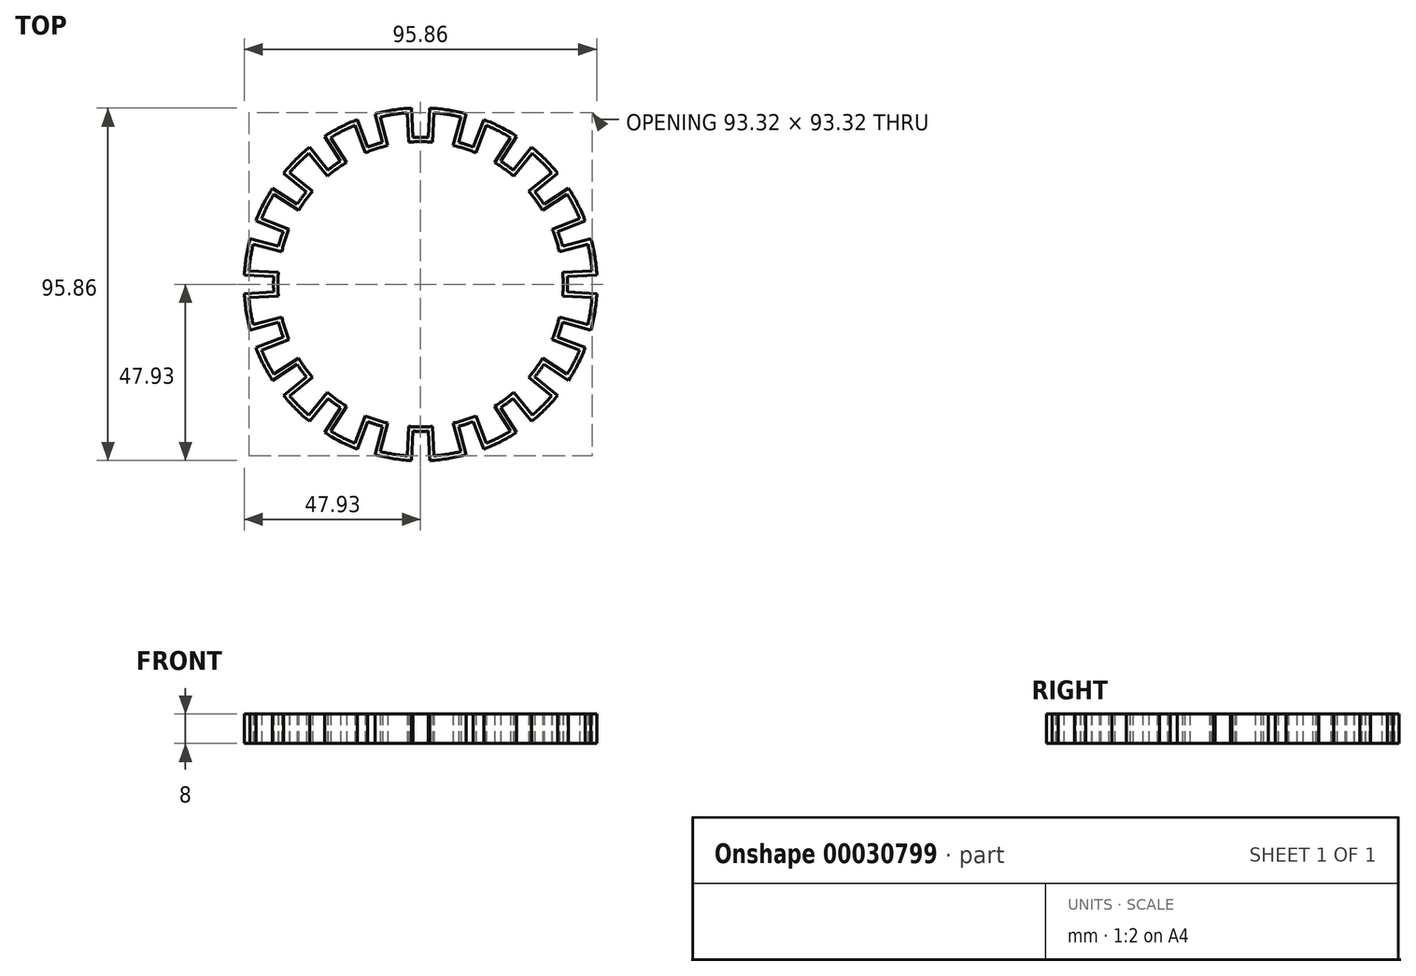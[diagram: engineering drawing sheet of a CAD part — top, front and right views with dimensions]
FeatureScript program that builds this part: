
annotation { "Feature Type Name" : "Feature", "Feature Type Description" : "" }
export const myFeature = defineFeature(function(context is Context, id is Id, definition is map)
    precondition{}
    {
        {
            var Q0;
            Q0=qCreatedBy(makeId("Top.planeOp"),FACE);
            var sketch = newSketch(context, id + "F0", { "sketchPlane" : qUnion([Q0])});
            skLineSegment(sketch, "E0", {"start": v(0, 40) * mm, "end": v(0, 0) * mm});
            skLineSegment(sketch, "E1", {"start": v(0, 0) * mm, "end": v(12.36, 38.04) * mm});
            skArc(sketch, "E2", {"start": v(12.42, 46.36) * mm, "mid": v(7.5, 47.4) * mm, "end": v(2.51, 47.93) * mm});
            skArc(sketch, "E3", {"start": v(12.36, 38.04) * mm, "mid": v(11.36, 38.35) * mm, "end": v(10.35, 38.64) * mm});
            skLineSegment(sketch, "E4", {"start": v(10.35, 38.64) * mm, "end": v(12.42, 46.36) * mm});
            skLineSegment(sketch, "E5", {"start": v(12.42, 46.36) * mm, "end": v(10.35, 38.64) * mm});
            skLineSegment(sketch, "E6", {"start": v(2.51, 47.93) * mm, "end": v(2.1, 39.95) * mm});
            skArc(sketch, "E7.trimOffspring", {"start": v(2.1, 39.95) * mm, "mid": v(1.05, 39.99) * mm, "end": v(0, 40) * mm});
            skPoint(sketch, "E8.start.orphan", {"position": v(0, 48) * mm});
            skSolve(sketch);
        }
        {
            var Q0;
            Q0 = qSketchRegion(id + "F0", true);
            extrude(context, id + "F1", {"entities" : qUnion([Q0]), "depth" : 8 * mm});
        }
        {
            var Q0;
            Q0=makeQuery(id+"F1.opExtrude","SWEPT_BODY",BODY,{"disambiguationData":[OSD([sQuery(id+"F0.wireOp",EDGE,"E0"),sQuery(id+"F0.wireOp",EDGE,"E1"),sQuery(id+"F0.wireOp",EDGE,"E2"),sQuery(id+"F0.wireOp",EDGE,"E3"),sQuery(id+"F0.wireOp",EDGE,"E5"),sQuery(id+"F0.wireOp",EDGE,"E6"),sQuery(id+"F0.wireOp",EDGE,"E7.trimOffspring")])]});
            var Q1;
            Q1=makeQuery(id+"F1.opExtrude","SWEPT_EDGE",EDGE,{"disambiguationData":[OSD([sQuery(id+"F0.wireOp",EDGE,"E0"),sQuery(id+"F0.wireOp",EDGE,"E1")])]});
            circularPattern(context, id + "F2", {"entities" : qUnion([Q0]), "axis" : qUnion([Q1]), "angle" : 18 * degree, "instanceCount" : 20});
        }
        {
            var Q0;
            Q0=makeQuery(id+"F2.opPattern","COPY",BODY,{"derivedFrom":makeQuery(id+"F1.opExtrude","SWEPT_BODY",BODY,{"disambiguationData":[OSD([sQuery(id+"F0.wireOp",EDGE,"E0"),sQuery(id+"F0.wireOp",EDGE,"E1"),sQuery(id+"F0.wireOp",EDGE,"E2"),sQuery(id+"F0.wireOp",EDGE,"E3"),sQuery(id+"F0.wireOp",EDGE,"E5"),sQuery(id+"F0.wireOp",EDGE,"E6"),sQuery(id+"F0.wireOp",EDGE,"E7.trimOffspring")])]}),"instanceName":"18"});
            var Q1;
            Q1=makeQuery(id+"F2.opPattern","COPY",BODY,{"derivedFrom":makeQuery(id+"F1.opExtrude","SWEPT_BODY",BODY,{"disambiguationData":[OSD([sQuery(id+"F0.wireOp",EDGE,"E0"),sQuery(id+"F0.wireOp",EDGE,"E1"),sQuery(id+"F0.wireOp",EDGE,"E2"),sQuery(id+"F0.wireOp",EDGE,"E3"),sQuery(id+"F0.wireOp",EDGE,"E5"),sQuery(id+"F0.wireOp",EDGE,"E6"),sQuery(id+"F0.wireOp",EDGE,"E7.trimOffspring")])]}),"instanceName":"19"});
            var Q2;
            Q2=makeQuery(id+"F1.opExtrude","SWEPT_BODY",BODY,{"disambiguationData":[OSD([sQuery(id+"F0.wireOp",EDGE,"E0"),sQuery(id+"F0.wireOp",EDGE,"E1"),sQuery(id+"F0.wireOp",EDGE,"E2"),sQuery(id+"F0.wireOp",EDGE,"E3"),sQuery(id+"F0.wireOp",EDGE,"E5"),sQuery(id+"F0.wireOp",EDGE,"E6"),sQuery(id+"F0.wireOp",EDGE,"E7.trimOffspring")])]});
            var Q3;
            Q3=makeQuery(id+"F2.opPattern","COPY",BODY,{"derivedFrom":makeQuery(id+"F1.opExtrude","SWEPT_BODY",BODY,{"disambiguationData":[OSD([sQuery(id+"F0.wireOp",EDGE,"E0"),sQuery(id+"F0.wireOp",EDGE,"E1"),sQuery(id+"F0.wireOp",EDGE,"E2"),sQuery(id+"F0.wireOp",EDGE,"E3"),sQuery(id+"F0.wireOp",EDGE,"E5"),sQuery(id+"F0.wireOp",EDGE,"E6"),sQuery(id+"F0.wireOp",EDGE,"E7.trimOffspring")])]}),"instanceName":"1"});
            var Q4;
            Q4=makeQuery(id+"F2.opPattern","COPY",BODY,{"derivedFrom":makeQuery(id+"F1.opExtrude","SWEPT_BODY",BODY,{"disambiguationData":[OSD([sQuery(id+"F0.wireOp",EDGE,"E0"),sQuery(id+"F0.wireOp",EDGE,"E1"),sQuery(id+"F0.wireOp",EDGE,"E2"),sQuery(id+"F0.wireOp",EDGE,"E3"),sQuery(id+"F0.wireOp",EDGE,"E5"),sQuery(id+"F0.wireOp",EDGE,"E6"),sQuery(id+"F0.wireOp",EDGE,"E7.trimOffspring")])]}),"instanceName":"2"});
            var Q5;
            Q5=makeQuery(id+"F2.opPattern","COPY",BODY,{"derivedFrom":makeQuery(id+"F1.opExtrude","SWEPT_BODY",BODY,{"disambiguationData":[OSD([sQuery(id+"F0.wireOp",EDGE,"E0"),sQuery(id+"F0.wireOp",EDGE,"E1"),sQuery(id+"F0.wireOp",EDGE,"E2"),sQuery(id+"F0.wireOp",EDGE,"E3"),sQuery(id+"F0.wireOp",EDGE,"E5"),sQuery(id+"F0.wireOp",EDGE,"E6"),sQuery(id+"F0.wireOp",EDGE,"E7.trimOffspring")])]}),"instanceName":"3"});
            var Q6;
            Q6=makeQuery(id+"F2.opPattern","COPY",BODY,{"derivedFrom":makeQuery(id+"F1.opExtrude","SWEPT_BODY",BODY,{"disambiguationData":[OSD([sQuery(id+"F0.wireOp",EDGE,"E0"),sQuery(id+"F0.wireOp",EDGE,"E1"),sQuery(id+"F0.wireOp",EDGE,"E2"),sQuery(id+"F0.wireOp",EDGE,"E3"),sQuery(id+"F0.wireOp",EDGE,"E5"),sQuery(id+"F0.wireOp",EDGE,"E6"),sQuery(id+"F0.wireOp",EDGE,"E7.trimOffspring")])]}),"instanceName":"4"});
            var Q7;
            Q7=makeQuery(id+"F2.opPattern","COPY",BODY,{"derivedFrom":makeQuery(id+"F1.opExtrude","SWEPT_BODY",BODY,{"disambiguationData":[OSD([sQuery(id+"F0.wireOp",EDGE,"E0"),sQuery(id+"F0.wireOp",EDGE,"E1"),sQuery(id+"F0.wireOp",EDGE,"E2"),sQuery(id+"F0.wireOp",EDGE,"E3"),sQuery(id+"F0.wireOp",EDGE,"E5"),sQuery(id+"F0.wireOp",EDGE,"E6"),sQuery(id+"F0.wireOp",EDGE,"E7.trimOffspring")])]}),"instanceName":"5"});
            var Q8;
            Q8=makeQuery(id+"F2.opPattern","COPY",BODY,{"derivedFrom":makeQuery(id+"F1.opExtrude","SWEPT_BODY",BODY,{"disambiguationData":[OSD([sQuery(id+"F0.wireOp",EDGE,"E0"),sQuery(id+"F0.wireOp",EDGE,"E1"),sQuery(id+"F0.wireOp",EDGE,"E2"),sQuery(id+"F0.wireOp",EDGE,"E3"),sQuery(id+"F0.wireOp",EDGE,"E5"),sQuery(id+"F0.wireOp",EDGE,"E6"),sQuery(id+"F0.wireOp",EDGE,"E7.trimOffspring")])]}),"instanceName":"6"});
            var Q9;
            Q9=makeQuery(id+"F2.opPattern","COPY",BODY,{"derivedFrom":makeQuery(id+"F1.opExtrude","SWEPT_BODY",BODY,{"disambiguationData":[OSD([sQuery(id+"F0.wireOp",EDGE,"E0"),sQuery(id+"F0.wireOp",EDGE,"E1"),sQuery(id+"F0.wireOp",EDGE,"E2"),sQuery(id+"F0.wireOp",EDGE,"E3"),sQuery(id+"F0.wireOp",EDGE,"E5"),sQuery(id+"F0.wireOp",EDGE,"E6"),sQuery(id+"F0.wireOp",EDGE,"E7.trimOffspring")])]}),"instanceName":"7"});
            var Q10;
            Q10=makeQuery(id+"F2.opPattern","COPY",BODY,{"derivedFrom":makeQuery(id+"F1.opExtrude","SWEPT_BODY",BODY,{"disambiguationData":[OSD([sQuery(id+"F0.wireOp",EDGE,"E0"),sQuery(id+"F0.wireOp",EDGE,"E1"),sQuery(id+"F0.wireOp",EDGE,"E2"),sQuery(id+"F0.wireOp",EDGE,"E3"),sQuery(id+"F0.wireOp",EDGE,"E5"),sQuery(id+"F0.wireOp",EDGE,"E6"),sQuery(id+"F0.wireOp",EDGE,"E7.trimOffspring")])]}),"instanceName":"8"});
            var Q11;
            Q11=makeQuery(id+"F2.opPattern","COPY",BODY,{"derivedFrom":makeQuery(id+"F1.opExtrude","SWEPT_BODY",BODY,{"disambiguationData":[OSD([sQuery(id+"F0.wireOp",EDGE,"E0"),sQuery(id+"F0.wireOp",EDGE,"E1"),sQuery(id+"F0.wireOp",EDGE,"E2"),sQuery(id+"F0.wireOp",EDGE,"E3"),sQuery(id+"F0.wireOp",EDGE,"E5"),sQuery(id+"F0.wireOp",EDGE,"E6"),sQuery(id+"F0.wireOp",EDGE,"E7.trimOffspring")])]}),"instanceName":"9"});
            var Q12;
            Q12=makeQuery(id+"F2.opPattern","COPY",BODY,{"derivedFrom":makeQuery(id+"F1.opExtrude","SWEPT_BODY",BODY,{"disambiguationData":[OSD([sQuery(id+"F0.wireOp",EDGE,"E0"),sQuery(id+"F0.wireOp",EDGE,"E1"),sQuery(id+"F0.wireOp",EDGE,"E2"),sQuery(id+"F0.wireOp",EDGE,"E3"),sQuery(id+"F0.wireOp",EDGE,"E5"),sQuery(id+"F0.wireOp",EDGE,"E6"),sQuery(id+"F0.wireOp",EDGE,"E7.trimOffspring")])]}),"instanceName":"10"});
            var Q13;
            Q13=makeQuery(id+"F2.opPattern","COPY",BODY,{"derivedFrom":makeQuery(id+"F1.opExtrude","SWEPT_BODY",BODY,{"disambiguationData":[OSD([sQuery(id+"F0.wireOp",EDGE,"E0"),sQuery(id+"F0.wireOp",EDGE,"E1"),sQuery(id+"F0.wireOp",EDGE,"E2"),sQuery(id+"F0.wireOp",EDGE,"E3"),sQuery(id+"F0.wireOp",EDGE,"E5"),sQuery(id+"F0.wireOp",EDGE,"E6"),sQuery(id+"F0.wireOp",EDGE,"E7.trimOffspring")])]}),"instanceName":"11"});
            var Q14;
            Q14=makeQuery(id+"F2.opPattern","COPY",BODY,{"derivedFrom":makeQuery(id+"F1.opExtrude","SWEPT_BODY",BODY,{"disambiguationData":[OSD([sQuery(id+"F0.wireOp",EDGE,"E0"),sQuery(id+"F0.wireOp",EDGE,"E1"),sQuery(id+"F0.wireOp",EDGE,"E2"),sQuery(id+"F0.wireOp",EDGE,"E3"),sQuery(id+"F0.wireOp",EDGE,"E5"),sQuery(id+"F0.wireOp",EDGE,"E6"),sQuery(id+"F0.wireOp",EDGE,"E7.trimOffspring")])]}),"instanceName":"12"});
            var Q15;
            Q15=makeQuery(id+"F2.opPattern","COPY",BODY,{"derivedFrom":makeQuery(id+"F1.opExtrude","SWEPT_BODY",BODY,{"disambiguationData":[OSD([sQuery(id+"F0.wireOp",EDGE,"E0"),sQuery(id+"F0.wireOp",EDGE,"E1"),sQuery(id+"F0.wireOp",EDGE,"E2"),sQuery(id+"F0.wireOp",EDGE,"E3"),sQuery(id+"F0.wireOp",EDGE,"E5"),sQuery(id+"F0.wireOp",EDGE,"E6"),sQuery(id+"F0.wireOp",EDGE,"E7.trimOffspring")])]}),"instanceName":"13"});
            var Q16;
            Q16=makeQuery(id+"F2.opPattern","COPY",BODY,{"derivedFrom":makeQuery(id+"F1.opExtrude","SWEPT_BODY",BODY,{"disambiguationData":[OSD([sQuery(id+"F0.wireOp",EDGE,"E0"),sQuery(id+"F0.wireOp",EDGE,"E1"),sQuery(id+"F0.wireOp",EDGE,"E2"),sQuery(id+"F0.wireOp",EDGE,"E3"),sQuery(id+"F0.wireOp",EDGE,"E5"),sQuery(id+"F0.wireOp",EDGE,"E6"),sQuery(id+"F0.wireOp",EDGE,"E7.trimOffspring")])]}),"instanceName":"14"});
            var Q17;
            Q17=makeQuery(id+"F2.opPattern","COPY",BODY,{"derivedFrom":makeQuery(id+"F1.opExtrude","SWEPT_BODY",BODY,{"disambiguationData":[OSD([sQuery(id+"F0.wireOp",EDGE,"E0"),sQuery(id+"F0.wireOp",EDGE,"E1"),sQuery(id+"F0.wireOp",EDGE,"E2"),sQuery(id+"F0.wireOp",EDGE,"E3"),sQuery(id+"F0.wireOp",EDGE,"E5"),sQuery(id+"F0.wireOp",EDGE,"E6"),sQuery(id+"F0.wireOp",EDGE,"E7.trimOffspring")])]}),"instanceName":"15"});
            var Q18;
            Q18=makeQuery(id+"F2.opPattern","COPY",BODY,{"derivedFrom":makeQuery(id+"F1.opExtrude","SWEPT_BODY",BODY,{"disambiguationData":[OSD([sQuery(id+"F0.wireOp",EDGE,"E0"),sQuery(id+"F0.wireOp",EDGE,"E1"),sQuery(id+"F0.wireOp",EDGE,"E2"),sQuery(id+"F0.wireOp",EDGE,"E3"),sQuery(id+"F0.wireOp",EDGE,"E5"),sQuery(id+"F0.wireOp",EDGE,"E6"),sQuery(id+"F0.wireOp",EDGE,"E7.trimOffspring")])]}),"instanceName":"16"});
            var Q19;
            Q19=makeQuery(id+"F2.opPattern","COPY",BODY,{"derivedFrom":makeQuery(id+"F1.opExtrude","SWEPT_BODY",BODY,{"disambiguationData":[OSD([sQuery(id+"F0.wireOp",EDGE,"E0"),sQuery(id+"F0.wireOp",EDGE,"E1"),sQuery(id+"F0.wireOp",EDGE,"E2"),sQuery(id+"F0.wireOp",EDGE,"E3"),sQuery(id+"F0.wireOp",EDGE,"E5"),sQuery(id+"F0.wireOp",EDGE,"E6"),sQuery(id+"F0.wireOp",EDGE,"E7.trimOffspring")])]}),"instanceName":"17"});
            booleanBodies(context, id + "F3", {"operationType" : BooleanOperationType.UNION, "tools" : qUnion([Q0, Q1, Q2, Q3, Q4, Q5, Q6, Q7, Q8, Q9, Q10, Q11, Q12, Q13, Q14, Q15, Q16, Q17, Q18, Q19])});
        }
        {
            var Q0;
            {var subQ0=makeQuery(id+"F1.opExtrude","CAP_FACE",FACE,{"disambiguationData":[OSD([sQuery(id+"F0.wireOp",EDGE,"E0"),sQuery(id+"F0.wireOp",EDGE,"E1"),sQuery(id+"F0.wireOp",EDGE,"E2"),sQuery(id+"F0.wireOp",EDGE,"E3"),sQuery(id+"F0.wireOp",EDGE,"E5"),sQuery(id+"F0.wireOp",EDGE,"E6"),sQuery(id+"F0.wireOp",EDGE,"E7.trimOffspring")])],"isStart":false});Q0=makeQuery(id+"F3.opBoolean","MERGE",FACE,{"derivedFrom":[subQ0,makeQuery(id+"F2.opPattern","COPY",FACE,{"derivedFrom":subQ0,"instanceName":"1"}),makeQuery(id+"F2.opPattern","COPY",FACE,{"derivedFrom":subQ0,"instanceName":"2"}),makeQuery(id+"F2.opPattern","COPY",FACE,{"derivedFrom":subQ0,"instanceName":"3"}),makeQuery(id+"F2.opPattern","COPY",FACE,{"derivedFrom":subQ0,"instanceName":"4"}),makeQuery(id+"F2.opPattern","COPY",FACE,{"derivedFrom":subQ0,"instanceName":"5"}),makeQuery(id+"F2.opPattern","COPY",FACE,{"derivedFrom":subQ0,"instanceName":"6"}),makeQuery(id+"F2.opPattern","COPY",FACE,{"derivedFrom":subQ0,"instanceName":"7"}),makeQuery(id+"F2.opPattern","COPY",FACE,{"derivedFrom":subQ0,"instanceName":"8"}),makeQuery(id+"F2.opPattern","COPY",FACE,{"derivedFrom":subQ0,"instanceName":"9"}),makeQuery(id+"F2.opPattern","COPY",FACE,{"derivedFrom":subQ0,"instanceName":"10"}),makeQuery(id+"F2.opPattern","COPY",FACE,{"derivedFrom":subQ0,"instanceName":"11"}),makeQuery(id+"F2.opPattern","COPY",FACE,{"derivedFrom":subQ0,"instanceName":"12"}),makeQuery(id+"F2.opPattern","COPY",FACE,{"derivedFrom":subQ0,"instanceName":"13"}),makeQuery(id+"F2.opPattern","COPY",FACE,{"derivedFrom":subQ0,"instanceName":"14"}),makeQuery(id+"F2.opPattern","COPY",FACE,{"derivedFrom":subQ0,"instanceName":"15"}),makeQuery(id+"F2.opPattern","COPY",FACE,{"derivedFrom":subQ0,"instanceName":"16"}),makeQuery(id+"F2.opPattern","COPY",FACE,{"derivedFrom":subQ0,"instanceName":"17"}),makeQuery(id+"F2.opPattern","COPY",FACE,{"derivedFrom":subQ0,"instanceName":"18"}),makeQuery(id+"F2.opPattern","COPY",FACE,{"derivedFrom":subQ0,"instanceName":"19"})]});}
            var Q1;
            {var subQ0=makeQuery(id+"F1.opExtrude","CAP_FACE",FACE,{"disambiguationData":[OSD([sQuery(id+"F0.wireOp",EDGE,"E0"),sQuery(id+"F0.wireOp",EDGE,"E1"),sQuery(id+"F0.wireOp",EDGE,"E2"),sQuery(id+"F0.wireOp",EDGE,"E3"),sQuery(id+"F0.wireOp",EDGE,"E5"),sQuery(id+"F0.wireOp",EDGE,"E6"),sQuery(id+"F0.wireOp",EDGE,"E7.trimOffspring")])],"isStart":true});Q1=makeQuery(id+"F3.opBoolean","MERGE",FACE,{"derivedFrom":[subQ0,makeQuery(id+"F2.opPattern","COPY",FACE,{"derivedFrom":subQ0,"instanceName":"1"}),makeQuery(id+"F2.opPattern","COPY",FACE,{"derivedFrom":subQ0,"instanceName":"2"}),makeQuery(id+"F2.opPattern","COPY",FACE,{"derivedFrom":subQ0,"instanceName":"3"}),makeQuery(id+"F2.opPattern","COPY",FACE,{"derivedFrom":subQ0,"instanceName":"4"}),makeQuery(id+"F2.opPattern","COPY",FACE,{"derivedFrom":subQ0,"instanceName":"5"}),makeQuery(id+"F2.opPattern","COPY",FACE,{"derivedFrom":subQ0,"instanceName":"6"}),makeQuery(id+"F2.opPattern","COPY",FACE,{"derivedFrom":subQ0,"instanceName":"7"}),makeQuery(id+"F2.opPattern","COPY",FACE,{"derivedFrom":subQ0,"instanceName":"8"}),makeQuery(id+"F2.opPattern","COPY",FACE,{"derivedFrom":subQ0,"instanceName":"9"}),makeQuery(id+"F2.opPattern","COPY",FACE,{"derivedFrom":subQ0,"instanceName":"10"}),makeQuery(id+"F2.opPattern","COPY",FACE,{"derivedFrom":subQ0,"instanceName":"11"}),makeQuery(id+"F2.opPattern","COPY",FACE,{"derivedFrom":subQ0,"instanceName":"12"}),makeQuery(id+"F2.opPattern","COPY",FACE,{"derivedFrom":subQ0,"instanceName":"13"}),makeQuery(id+"F2.opPattern","COPY",FACE,{"derivedFrom":subQ0,"instanceName":"14"}),makeQuery(id+"F2.opPattern","COPY",FACE,{"derivedFrom":subQ0,"instanceName":"15"}),makeQuery(id+"F2.opPattern","COPY",FACE,{"derivedFrom":subQ0,"instanceName":"16"}),makeQuery(id+"F2.opPattern","COPY",FACE,{"derivedFrom":subQ0,"instanceName":"17"}),makeQuery(id+"F2.opPattern","COPY",FACE,{"derivedFrom":subQ0,"instanceName":"18"}),makeQuery(id+"F2.opPattern","COPY",FACE,{"derivedFrom":subQ0,"instanceName":"19"})]});}
            shell(context, id + "F4", {"entities" : qUnion([Q0, Q1]), "thickness" : 1.2 * mm});
        }
    });
